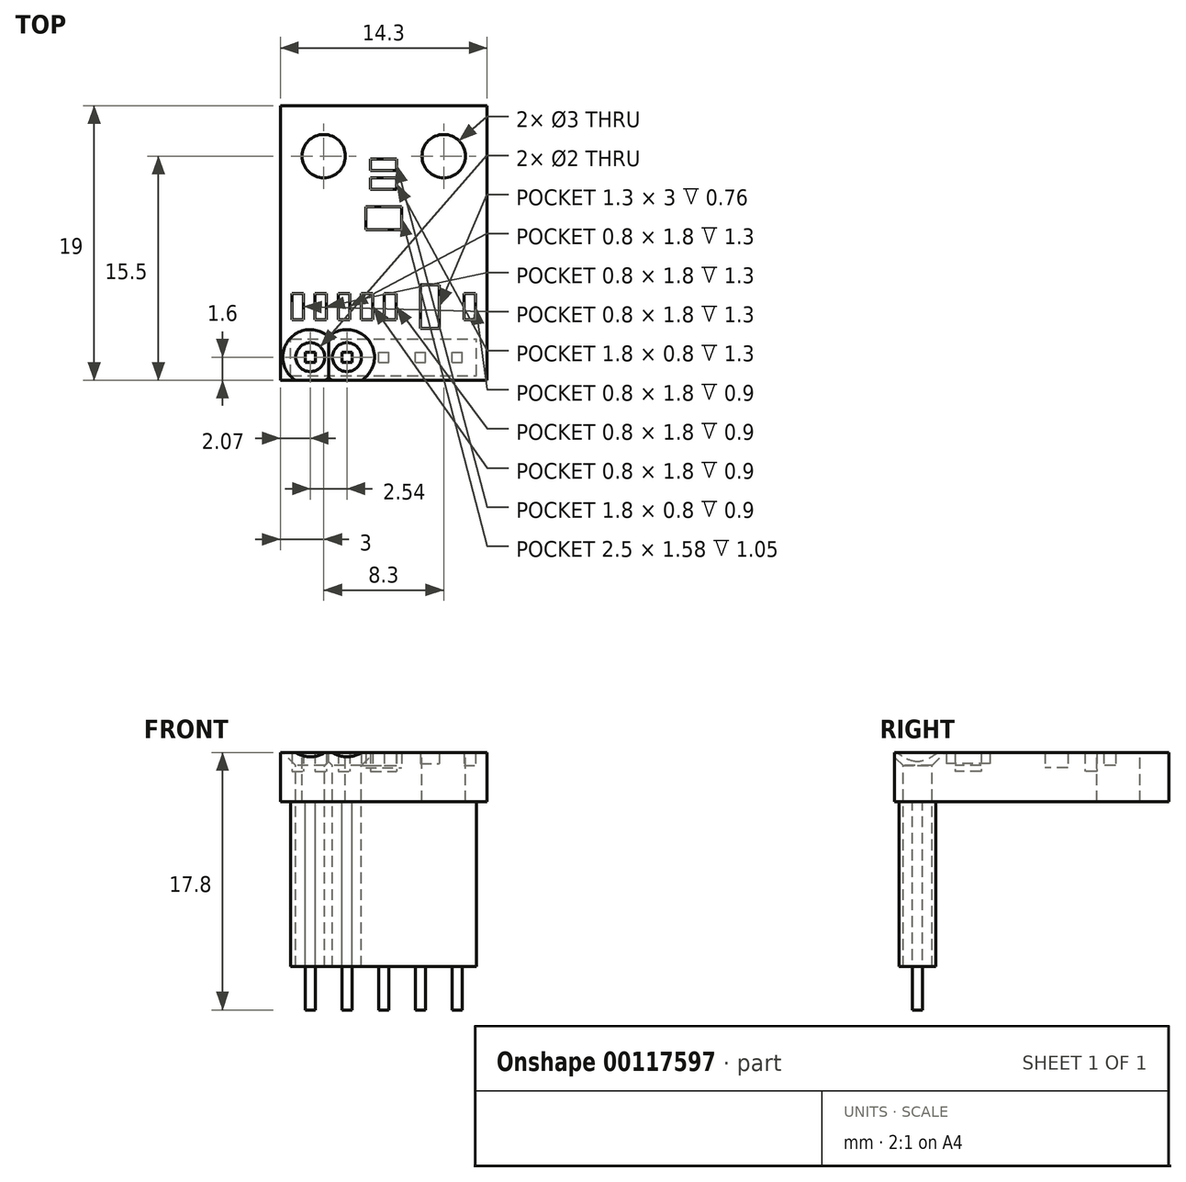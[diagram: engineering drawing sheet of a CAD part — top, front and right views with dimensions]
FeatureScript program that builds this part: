
annotation { "Feature Type Name" : "Feature", "Feature Type Description" : "" }
export const myFeature = defineFeature(function(context is Context, id is Id, definition is map)
    precondition{}
    {
        {
            var Q0;
            Q0=qCreatedBy(makeId("Top.planeOp"),FACE);
            var sketch = newSketch(context, id + "F0", { "sketchPlane" : qUnion([Q0])});
            skLineSegment(sketch, "E0.bottom", {"start": v(-7.15, 9.5) * mm, "end": v(7.15, 9.5) * mm});
            skLineSegment(sketch, "E0.top", {"start": v(-7.15, -9.5) * mm, "end": v(7.15, -9.5) * mm});
            skLineSegment(sketch, "E0.left", {"start": v(-7.15, 9.5) * mm, "end": v(-7.15, -9.5) * mm});
            skLineSegment(sketch, "E0.right", {"start": v(7.15, 9.5) * mm, "end": v(7.15, -9.5) * mm});
            skLineSegment(sketch, "E1", {"start": v(0, 9.5) * mm, "end": v(0, -9.5) * mm, "construction": true});
            skLineSegment(sketch, "E2", {"start": v(-7.15, 0) * mm, "end": v(7.15, 0) * mm, "construction": true});
            skCircle(sketch, "E3", {"center": v(-4.15, 6) * mm, "radius": 1.5 * mm});
            skCircle(sketch, "E4.MirrorC", {"center": v(4.15, 6) * mm, "radius": 1.5 * mm});
            skLineSegment(sketch, "E5.bottom", {"start": v(-1.25, 2.5) * mm, "end": v(1.25, 2.5) * mm});
            skLineSegment(sketch, "E5.top", {"start": v(-1.25, 0.92) * mm, "end": v(1.25, 0.92) * mm});
            skLineSegment(sketch, "E5.left", {"start": v(-1.25, 2.5) * mm, "end": v(-1.25, 0.92) * mm});
            skLineSegment(sketch, "E5.right", {"start": v(1.25, 2.5) * mm, "end": v(1.25, 0.92) * mm});
            skLineSegment(sketch, "E6.bottom", {"start": v(-0.9, 5.8) * mm, "end": v(0.9, 5.8) * mm});
            skLineSegment(sketch, "E6.top", {"start": v(-0.9, 5) * mm, "end": v(0.9, 5) * mm});
            skLineSegment(sketch, "E6.left", {"start": v(-0.9, 5.8) * mm, "end": v(-0.9, 5) * mm});
            skLineSegment(sketch, "E6.right", {"start": v(0.9, 5.8) * mm, "end": v(0.9, 5) * mm});
            skLineSegment(sketch, "E7.bottom", {"start": v(-0.9, 4.5) * mm, "end": v(0.9, 4.5) * mm});
            skLineSegment(sketch, "E7.top", {"start": v(-0.9, 3.7) * mm, "end": v(0.9, 3.7) * mm});
            skLineSegment(sketch, "E7.left", {"start": v(-0.9, 4.5) * mm, "end": v(-0.9, 3.7) * mm});
            skLineSegment(sketch, "E7.right", {"start": v(0.9, 4.5) * mm, "end": v(0.9, 3.7) * mm});
            skLineSegment(sketch, "E8.bottom", {"start": v(-6.35, -3.5) * mm, "end": v(-5.55, -3.5) * mm});
            skLineSegment(sketch, "E8.top", {"start": v(-6.35, -5.3) * mm, "end": v(-5.55, -5.3) * mm});
            skLineSegment(sketch, "E8.left", {"start": v(-6.35, -3.5) * mm, "end": v(-6.35, -5.3) * mm});
            skLineSegment(sketch, "E8.right", {"start": v(-5.55, -3.5) * mm, "end": v(-5.55, -5.3) * mm});
            skLineSegment(sketch, "E9.bottom", {"start": v(-4.75, -3.5) * mm, "end": v(-3.95, -3.5) * mm});
            skLineSegment(sketch, "E9.top", {"start": v(-4.75, -5.3) * mm, "end": v(-3.95, -5.3) * mm});
            skLineSegment(sketch, "E9.left", {"start": v(-4.75, -3.5) * mm, "end": v(-4.75, -5.3) * mm});
            skLineSegment(sketch, "E9.right", {"start": v(-3.95, -3.5) * mm, "end": v(-3.95, -5.3) * mm});
            skLineSegment(sketch, "E10.bottom", {"start": v(-3.15, -3.5) * mm, "end": v(-2.35, -3.5) * mm});
            skLineSegment(sketch, "E10.top", {"start": v(-3.15, -5.3) * mm, "end": v(-2.35, -5.3) * mm});
            skLineSegment(sketch, "E10.left", {"start": v(-3.15, -3.5) * mm, "end": v(-3.15, -5.3) * mm});
            skLineSegment(sketch, "E10.right", {"start": v(-2.35, -3.5) * mm, "end": v(-2.35, -5.3) * mm});
            skLineSegment(sketch, "E11.bottom", {"start": v(-1.55, -3.5) * mm, "end": v(-0.75, -3.5) * mm});
            skLineSegment(sketch, "E11.top", {"start": v(-1.55, -5.3) * mm, "end": v(-0.75, -5.3) * mm});
            skLineSegment(sketch, "E11.left", {"start": v(-1.55, -3.5) * mm, "end": v(-1.55, -5.3) * mm});
            skLineSegment(sketch, "E11.right", {"start": v(-0.75, -3.5) * mm, "end": v(-0.75, -5.3) * mm});
            skLineSegment(sketch, "E12.bottom", {"start": v(0.05, -3.5) * mm, "end": v(0.85, -3.5) * mm});
            skLineSegment(sketch, "E12.top", {"start": v(0.05, -5.3) * mm, "end": v(0.85, -5.3) * mm});
            skLineSegment(sketch, "E12.left", {"start": v(0.05, -3.5) * mm, "end": v(0.05, -5.3) * mm});
            skLineSegment(sketch, "E12.right", {"start": v(0.85, -3.5) * mm, "end": v(0.85, -5.3) * mm});
            skLineSegment(sketch, "E13.bottom", {"start": v(2.55, -2.9) * mm, "end": v(3.85, -2.9) * mm});
            skLineSegment(sketch, "E13.top", {"start": v(2.55, -5.9) * mm, "end": v(3.85, -5.9) * mm});
            skLineSegment(sketch, "E13.left", {"start": v(2.55, -2.9) * mm, "end": v(2.55, -5.9) * mm});
            skLineSegment(sketch, "E13.right", {"start": v(3.85, -2.9) * mm, "end": v(3.85, -5.9) * mm});
            skLineSegment(sketch, "E14.bottom", {"start": v(5.55, -3.5) * mm, "end": v(6.35, -3.5) * mm});
            skLineSegment(sketch, "E14.top", {"start": v(5.55, -5.3) * mm, "end": v(6.35, -5.3) * mm});
            skLineSegment(sketch, "E14.left", {"start": v(5.55, -3.5) * mm, "end": v(5.55, -5.3) * mm});
            skLineSegment(sketch, "E14.right", {"start": v(6.35, -3.5) * mm, "end": v(6.35, -5.3) * mm});
            skLineSegment(sketch, "E15", {"start": v(7.15, -4.4) * mm, "end": v(-7.15, -4.4) * mm, "construction": true});
            skArc(sketch, "E16", {"start": v(0, -8.9) * mm, "mid": v(1, -7.9) * mm, "end": v(0, -6.9) * mm});
            skCircle(sketch, "E17", {"center": v(2.54, -7.9) * mm, "radius": 1 * mm});
            skCircle(sketch, "E18", {"center": v(5.08, -7.9) * mm, "radius": 1 * mm});
            skArc(sketch, "E19.MirrorCS", {"start": v(0, -8.9) * mm, "mid": v(-1, -7.9) * mm, "end": v(0, -6.9) * mm});
            skCircle(sketch, "E20.MirrorC", {"center": v(-2.54, -7.9) * mm, "radius": 1 * mm});
            skCircle(sketch, "E21.MirrorC", {"center": v(-5.08, -7.9) * mm, "radius": 1 * mm});
            skSolve(sketch);
        }
        {
            var Q0;
            Q0=makeQuery(id+"F0.imprint","IMPRINT",FACE,{"disambiguationData":[TD([[makeQuery(id+"F0.imprint","IMPRINT",EDGE,{"derivedFrom":sQuery(id+"F0.wireOp",EDGE,"E0.bottom")}),-1.0]])]});
            var Q1;
            Q1=makeQuery(id+"F0.imprint","IMPRINT",FACE,{"disambiguationData":[TD([[makeQuery(id+"F0.imprint","IMPRINT",EDGE,{"derivedFrom":sQuery(id+"F0.wireOp",EDGE,"E5.bottom")}),-1.0]])]});
            var Q2;
            Q2=makeQuery(id+"F0.imprint","IMPRINT",FACE,{"disambiguationData":[TD([[makeQuery(id+"F0.imprint","IMPRINT",EDGE,{"derivedFrom":sQuery(id+"F0.wireOp",EDGE,"E14.bottom")}),-1.0]])]});
            var Q3;
            Q3=makeQuery(id+"F0.imprint","IMPRINT",FACE,{"disambiguationData":[TD([[makeQuery(id+"F0.imprint","IMPRINT",EDGE,{"derivedFrom":sQuery(id+"F0.wireOp",EDGE,"E13.bottom")}),-1.0]])]});
            var Q4;
            Q4=makeQuery(id+"F0.imprint","IMPRINT",FACE,{"disambiguationData":[TD([[makeQuery(id+"F0.imprint","IMPRINT",EDGE,{"derivedFrom":sQuery(id+"F0.wireOp",EDGE,"E12.bottom")}),-1.0]])]});
            var Q5;
            Q5=makeQuery(id+"F0.imprint","IMPRINT",FACE,{"disambiguationData":[TD([[makeQuery(id+"F0.imprint","IMPRINT",EDGE,{"derivedFrom":sQuery(id+"F0.wireOp",EDGE,"E11.bottom")}),-1.0]])]});
            var Q6;
            Q6=makeQuery(id+"F0.imprint","IMPRINT",FACE,{"disambiguationData":[TD([[makeQuery(id+"F0.imprint","IMPRINT",EDGE,{"derivedFrom":sQuery(id+"F0.wireOp",EDGE,"E10.bottom")}),-1.0]])]});
            var Q7;
            Q7=makeQuery(id+"F0.imprint","IMPRINT",FACE,{"disambiguationData":[TD([[makeQuery(id+"F0.imprint","IMPRINT",EDGE,{"derivedFrom":sQuery(id+"F0.wireOp",EDGE,"E9.bottom")}),-1.0]])]});
            var Q8;
            Q8=makeQuery(id+"F0.imprint","IMPRINT",FACE,{"disambiguationData":[TD([[makeQuery(id+"F0.imprint","IMPRINT",EDGE,{"derivedFrom":sQuery(id+"F0.wireOp",EDGE,"E8.bottom")}),-1.0]])]});
            var Q9;
            Q9=makeQuery(id+"F0.imprint","IMPRINT",FACE,{"disambiguationData":[TD([[makeQuery(id+"F0.imprint","IMPRINT",EDGE,{"derivedFrom":sQuery(id+"F0.wireOp",EDGE,"E7.bottom")}),-1.0]])]});
            var Q10;
            Q10=makeQuery(id+"F0.imprint","IMPRINT",FACE,{"disambiguationData":[TD([[makeQuery(id+"F0.imprint","IMPRINT",EDGE,{"derivedFrom":sQuery(id+"F0.wireOp",EDGE,"E6.bottom")}),-1.0]])]});
            var Q11;
            Q11=makeQuery(id+"F0.imprint","IMPRINT",FACE,{"disambiguationData":[TD([[makeQuery(id+"F0.imprint","IMPRINT",EDGE,{"derivedFrom":sQuery(id+"F0.wireOp",EDGE,"E21.MirrorC")}),-1.0]])]});
            var Q12;
            Q12=makeQuery(id+"F0.imprint","IMPRINT",FACE,{"disambiguationData":[TD([[makeQuery(id+"F0.imprint","IMPRINT",EDGE,{"derivedFrom":sQuery(id+"F0.wireOp",EDGE,"E20.MirrorC")}),-1.0]])]});
            var Q13;
            Q13=makeQuery(id+"F0.imprint","IMPRINT",FACE,{"disambiguationData":[TD([[makeQuery(id+"F0.imprint","IMPRINT",EDGE,{"derivedFrom":sQuery(id+"F0.wireOp",EDGE,"E16")}),1.0]])]});
            var Q14;
            Q14=makeQuery(id+"F0.imprint","IMPRINT",FACE,{"disambiguationData":[TD([[makeQuery(id+"F0.imprint","IMPRINT",EDGE,{"derivedFrom":sQuery(id+"F0.wireOp",EDGE,"E17")}),1.0]])]});
            var Q15;
            Q15=makeQuery(id+"F0.imprint","IMPRINT",FACE,{"disambiguationData":[TD([[makeQuery(id+"F0.imprint","IMPRINT",EDGE,{"derivedFrom":sQuery(id+"F0.wireOp",EDGE,"E18")}),1.0]])]});
            extrude(context, id + "F1", {"entities" : qUnion([Q0, Q1, Q2, Q3, Q4, Q5, Q6, Q7, Q8, Q9, Q10, Q11, Q12, Q13, Q14, Q15]), "oppositeDirection" : true, "depth" : 1.6 * mm});
        }
        {
            var Q0;
            Q0=makeQuery(id+"F0.imprint","IMPRINT",FACE,{"disambiguationData":[TD([[makeQuery(id+"F0.imprint","IMPRINT",EDGE,{"derivedFrom":sQuery(id+"F0.wireOp",EDGE,"E5.bottom")}),-1.0]])]});
            extrude(context, id + "F2", {"entities" : qUnion([Q0]), "operationType" : NewBodyOperationType.ADD, "depth" : 0.75 * mm});
        }
        {
            var Q0;
            Q0=makeQuery(id+"F0.imprint","IMPRINT",FACE,{"disambiguationData":[TD([[makeQuery(id+"F0.imprint","IMPRINT",EDGE,{"derivedFrom":sQuery(id+"F0.wireOp",EDGE,"E6.bottom")}),-1.0]])]});
            var Q1;
            Q1=makeQuery(id+"F0.imprint","IMPRINT",FACE,{"disambiguationData":[TD([[makeQuery(id+"F0.imprint","IMPRINT",EDGE,{"derivedFrom":sQuery(id+"F0.wireOp",EDGE,"E14.bottom")}),-1.0]])]});
            var Q2;
            Q2=makeQuery(id+"F0.imprint","IMPRINT",FACE,{"disambiguationData":[TD([[makeQuery(id+"F0.imprint","IMPRINT",EDGE,{"derivedFrom":sQuery(id+"F0.wireOp",EDGE,"E12.bottom")}),-1.0]])]});
            var Q3;
            Q3=makeQuery(id+"F0.imprint","IMPRINT",FACE,{"disambiguationData":[TD([[makeQuery(id+"F0.imprint","IMPRINT",EDGE,{"derivedFrom":sQuery(id+"F0.wireOp",EDGE,"E11.bottom")}),-1.0]])]});
            extrude(context, id + "F3", {"entities" : qUnion([Q0, Q1, Q2, Q3]), "operationType" : NewBodyOperationType.ADD, "depth" : 0.9 * mm});
        }
        {
            var Q0;
            Q0=makeQuery(id+"F0.imprint","IMPRINT",FACE,{"disambiguationData":[TD([[makeQuery(id+"F0.imprint","IMPRINT",EDGE,{"derivedFrom":sQuery(id+"F0.wireOp",EDGE,"E7.bottom")}),-1.0]])]});
            var Q1;
            Q1=makeQuery(id+"F0.imprint","IMPRINT",FACE,{"disambiguationData":[TD([[makeQuery(id+"F0.imprint","IMPRINT",EDGE,{"derivedFrom":sQuery(id+"F0.wireOp",EDGE,"E10.bottom")}),-1.0]])]});
            var Q2;
            Q2=makeQuery(id+"F0.imprint","IMPRINT",FACE,{"disambiguationData":[TD([[makeQuery(id+"F0.imprint","IMPRINT",EDGE,{"derivedFrom":sQuery(id+"F0.wireOp",EDGE,"E9.bottom")}),-1.0]])]});
            var Q3;
            Q3=makeQuery(id+"F0.imprint","IMPRINT",FACE,{"disambiguationData":[TD([[makeQuery(id+"F0.imprint","IMPRINT",EDGE,{"derivedFrom":sQuery(id+"F0.wireOp",EDGE,"E8.bottom")}),-1.0]])]});
            extrude(context, id + "F4", {"entities" : qUnion([Q0, Q1, Q2, Q3]), "operationType" : NewBodyOperationType.ADD, "depth" : 0.5 * mm});
        }
        {
            var Q0;
            Q0=makeQuery(id+"F0.imprint","IMPRINT",FACE,{"disambiguationData":[TD([[makeQuery(id+"F0.imprint","IMPRINT",EDGE,{"derivedFrom":sQuery(id+"F0.wireOp",EDGE,"E13.bottom")}),-1.0]])]});
            extrude(context, id + "F5", {"entities" : qUnion([Q0]), "operationType" : NewBodyOperationType.ADD, "depth" : 1.04 * mm});
        }
        {
            var Q0;
            Q0=makeQuery(id+"F0.imprint","IMPRINT",FACE,{"disambiguationData":[TD([[makeQuery(id+"F0.imprint","IMPRINT",EDGE,{"derivedFrom":sQuery(id+"F0.wireOp",EDGE,"E21.MirrorC")}),-1.0]])]});
            var Q1;
            Q1=makeQuery(id+"F0.imprint","IMPRINT",FACE,{"disambiguationData":[TD([[makeQuery(id+"F0.imprint","IMPRINT",EDGE,{"derivedFrom":sQuery(id+"F0.wireOp",EDGE,"E20.MirrorC")}),-1.0]])]});
            var Q2;
            Q2=makeQuery(id+"F0.imprint","IMPRINT",FACE,{"disambiguationData":[TD([[makeQuery(id+"F0.imprint","IMPRINT",EDGE,{"derivedFrom":sQuery(id+"F0.wireOp",EDGE,"E16")}),1.0]])]});
            var Q3;
            Q3=makeQuery(id+"F0.imprint","IMPRINT",FACE,{"disambiguationData":[TD([[makeQuery(id+"F0.imprint","IMPRINT",EDGE,{"derivedFrom":sQuery(id+"F0.wireOp",EDGE,"E17")}),1.0]])]});
            var Q4;
            Q4=makeQuery(id+"F0.imprint","IMPRINT",FACE,{"disambiguationData":[TD([[makeQuery(id+"F0.imprint","IMPRINT",EDGE,{"derivedFrom":sQuery(id+"F0.wireOp",EDGE,"E18")}),1.0]])]});
            extrude(context, id + "F6", {"entities" : qUnion([Q0, Q1, Q2, Q3, Q4]), "operationType" : NewBodyOperationType.ADD, "depth" : 1.8 * mm});
        }
        {
            var Q0;
            Q0=makeQuery(id+"F6.opExtrude","CAP_EDGE",EDGE,{"disambiguationData":[OSD([sQuery(id+"F0.wireOp",EDGE,"E21.MirrorC")])],"isStart":false});
            var Q1;
            Q1=makeQuery(id+"F6.opExtrude","CAP_EDGE",EDGE,{"disambiguationData":[OSD([sQuery(id+"F0.wireOp",EDGE,"E20.MirrorC")])],"isStart":false});
            var Q2;
            Q2=makeQuery(id+"F6.opExtrude","CAP_EDGE",EDGE,{"disambiguationData":[OSD([sQuery(id+"F0.wireOp",EDGE,"E16"),sQuery(id+"F0.wireOp",EDGE,"E19.MirrorCS")])],"isStart":false});
            var Q3;
            Q3=makeQuery(id+"F6.opExtrude","CAP_EDGE",EDGE,{"disambiguationData":[OSD([sQuery(id+"F0.wireOp",EDGE,"E17")])],"isStart":false});
            var Q4;
            Q4=makeQuery(id+"F6.opExtrude","CAP_EDGE",EDGE,{"disambiguationData":[OSD([sQuery(id+"F0.wireOp",EDGE,"E18")])],"isStart":false});
            chamfer(context, id + "F7", {"entities" : qUnion([Q0, Q1, Q2, Q3, Q4]), "chamferType" : ChamferType.OFFSET_ANGLE, "width" : 0.9 * mm, "oppositeDirection" : false, "angle" : 45 * degree, "tangentPropagation" : true});
        }
        {
            var Q0;
            Q0=makeQuery(id+"F1.opExtrude","CAP_FACE",FACE,{"disambiguationData":[OSD([sQuery(id+"F0.wireOp",EDGE,"E0.bottom"),sQuery(id+"F0.wireOp",EDGE,"E0.top"),sQuery(id+"F0.wireOp",EDGE,"E0.left"),sQuery(id+"F0.wireOp",EDGE,"E0.right"),sQuery(id+"F0.wireOp",EDGE,"E3"),sQuery(id+"F0.wireOp",EDGE,"E4.MirrorC")])],"isStart":false});
            var sketch = newSketch(context, id + "F8", { "sketchPlane" : qUnion([Q0])});
            skLineSegment(sketch, "E22.bottom", {"start": v(-6.43, 9.17) * mm, "end": v(6.43, 9.17) * mm});
            skLineSegment(sketch, "E22.top", {"start": v(-6.43, 6.63) * mm, "end": v(6.43, 6.63) * mm});
            skLineSegment(sketch, "E22.left", {"start": v(-6.43, 9.17) * mm, "end": v(-6.43, 6.63) * mm});
            skLineSegment(sketch, "E22.right", {"start": v(6.43, 9.17) * mm, "end": v(6.43, 6.63) * mm});
            skLineSegment(sketch, "E23", {"start": v(-7.15, 7.9) * mm, "end": v(7.15, 7.9) * mm, "construction": true});
            skLineSegment(sketch, "E24.bottom", {"start": v(-5.43, 8.25) * mm, "end": v(-4.73, 8.25) * mm});
            skLineSegment(sketch, "E24.top", {"start": v(-5.43, 7.55) * mm, "end": v(-4.73, 7.55) * mm});
            skLineSegment(sketch, "E24.left", {"start": v(-5.43, 8.25) * mm, "end": v(-5.43, 7.55) * mm});
            skLineSegment(sketch, "E24.right", {"start": v(-4.73, 8.25) * mm, "end": v(-4.73, 7.55) * mm});
            skLineSegment(sketch, "E25", {"start": v(-5.08, 9.17) * mm, "end": v(-5.08, 6.63) * mm, "construction": true});
            skLineSegment(sketch, "E26", {"start": v(-2.54, 9.17) * mm, "end": v(-2.54, 6.63) * mm, "construction": true});
            skLineSegment(sketch, "E27", {"start": v(0, 9.17) * mm, "end": v(0, 6.63) * mm, "construction": true});
            skLineSegment(sketch, "E28", {"start": v(2.54, 9.17) * mm, "end": v(2.54, 6.63) * mm, "construction": true});
            skLineSegment(sketch, "E29", {"start": v(5.08, 9.17) * mm, "end": v(5.08, 6.63) * mm, "construction": true});
            skLineSegment(sketch, "E30.bottom", {"start": v(-2.9, 8.25) * mm, "end": v(-2.2, 8.25) * mm});
            skLineSegment(sketch, "E30.top", {"start": v(-2.9, 7.55) * mm, "end": v(-2.2, 7.55) * mm});
            skLineSegment(sketch, "E30.left", {"start": v(-2.9, 8.25) * mm, "end": v(-2.9, 7.55) * mm});
            skLineSegment(sketch, "E30.right", {"start": v(-2.2, 8.25) * mm, "end": v(-2.2, 7.55) * mm});
            skLineSegment(sketch, "E31.bottom", {"start": v(-0.35, 8.25) * mm, "end": v(0.35, 8.25) * mm});
            skLineSegment(sketch, "E31.top", {"start": v(-0.35, 7.55) * mm, "end": v(0.35, 7.55) * mm});
            skLineSegment(sketch, "E31.left", {"start": v(-0.35, 8.25) * mm, "end": v(-0.35, 7.55) * mm});
            skLineSegment(sketch, "E31.right", {"start": v(0.35, 8.25) * mm, "end": v(0.35, 7.55) * mm});
            skLineSegment(sketch, "E32.bottom", {"start": v(2.2, 8.25) * mm, "end": v(2.9, 8.25) * mm});
            skLineSegment(sketch, "E32.top", {"start": v(2.2, 7.55) * mm, "end": v(2.9, 7.55) * mm});
            skLineSegment(sketch, "E32.left", {"start": v(2.2, 8.25) * mm, "end": v(2.2, 7.55) * mm});
            skLineSegment(sketch, "E32.right", {"start": v(2.9, 8.25) * mm, "end": v(2.9, 7.55) * mm});
            skLineSegment(sketch, "E33.bottom", {"start": v(4.73, 8.25) * mm, "end": v(5.43, 8.25) * mm});
            skLineSegment(sketch, "E33.top", {"start": v(4.73, 7.55) * mm, "end": v(5.43, 7.55) * mm});
            skLineSegment(sketch, "E33.left", {"start": v(4.73, 8.25) * mm, "end": v(4.73, 7.55) * mm});
            skLineSegment(sketch, "E33.right", {"start": v(5.43, 8.25) * mm, "end": v(5.43, 7.55) * mm});
            skSolve(sketch);
        }
        {
            var Q0;
            Q0=makeQuery(id+"F8.imprint","IMPRINT",FACE,{"disambiguationData":[TD([[makeQuery(id+"F8.imprint","IMPRINT",EDGE,{"derivedFrom":sQuery(id+"F8.wireOp",EDGE,"E24.bottom")}),-1.0]])]});
            var Q1;
            Q1=makeQuery(id+"F8.imprint","IMPRINT",FACE,{"disambiguationData":[TD([[makeQuery(id+"F8.imprint","IMPRINT",EDGE,{"derivedFrom":sQuery(id+"F8.wireOp",EDGE,"E30.bottom")}),-1.0]])]});
            var Q2;
            Q2=makeQuery(id+"F8.imprint","IMPRINT",FACE,{"disambiguationData":[TD([[makeQuery(id+"F8.imprint","IMPRINT",EDGE,{"derivedFrom":sQuery(id+"F8.wireOp",EDGE,"E31.bottom")}),-1.0]])]});
            var Q3;
            Q3=makeQuery(id+"F8.imprint","IMPRINT",FACE,{"disambiguationData":[TD([[makeQuery(id+"F8.imprint","IMPRINT",EDGE,{"derivedFrom":sQuery(id+"F8.wireOp",EDGE,"E32.bottom")}),-1.0]])]});
            var Q4;
            Q4=makeQuery(id+"F8.imprint","IMPRINT",FACE,{"disambiguationData":[TD([[makeQuery(id+"F8.imprint","IMPRINT",EDGE,{"derivedFrom":sQuery(id+"F8.wireOp",EDGE,"E33.bottom")}),-1.0]])]});
            extrude(context, id + "F9", {"entities" : qUnion([Q0, Q1, Q2, Q3, Q4]), "operationType" : NewBodyOperationType.ADD, "depth" : 14.4 * mm});
        }
        {
            var Q0;
            Q0=makeQuery(id+"F8.imprint","IMPRINT",FACE,{"disambiguationData":[TD([[makeQuery(id+"F8.imprint","IMPRINT",EDGE,{"derivedFrom":sQuery(id+"F8.wireOp",EDGE,"E22.bottom")}),-1.0]])]});
            extrude(context, id + "F10", {"entities" : qUnion([Q0]), "operationType" : NewBodyOperationType.ADD, "depth" : 11.4 * mm});
        }
    });
